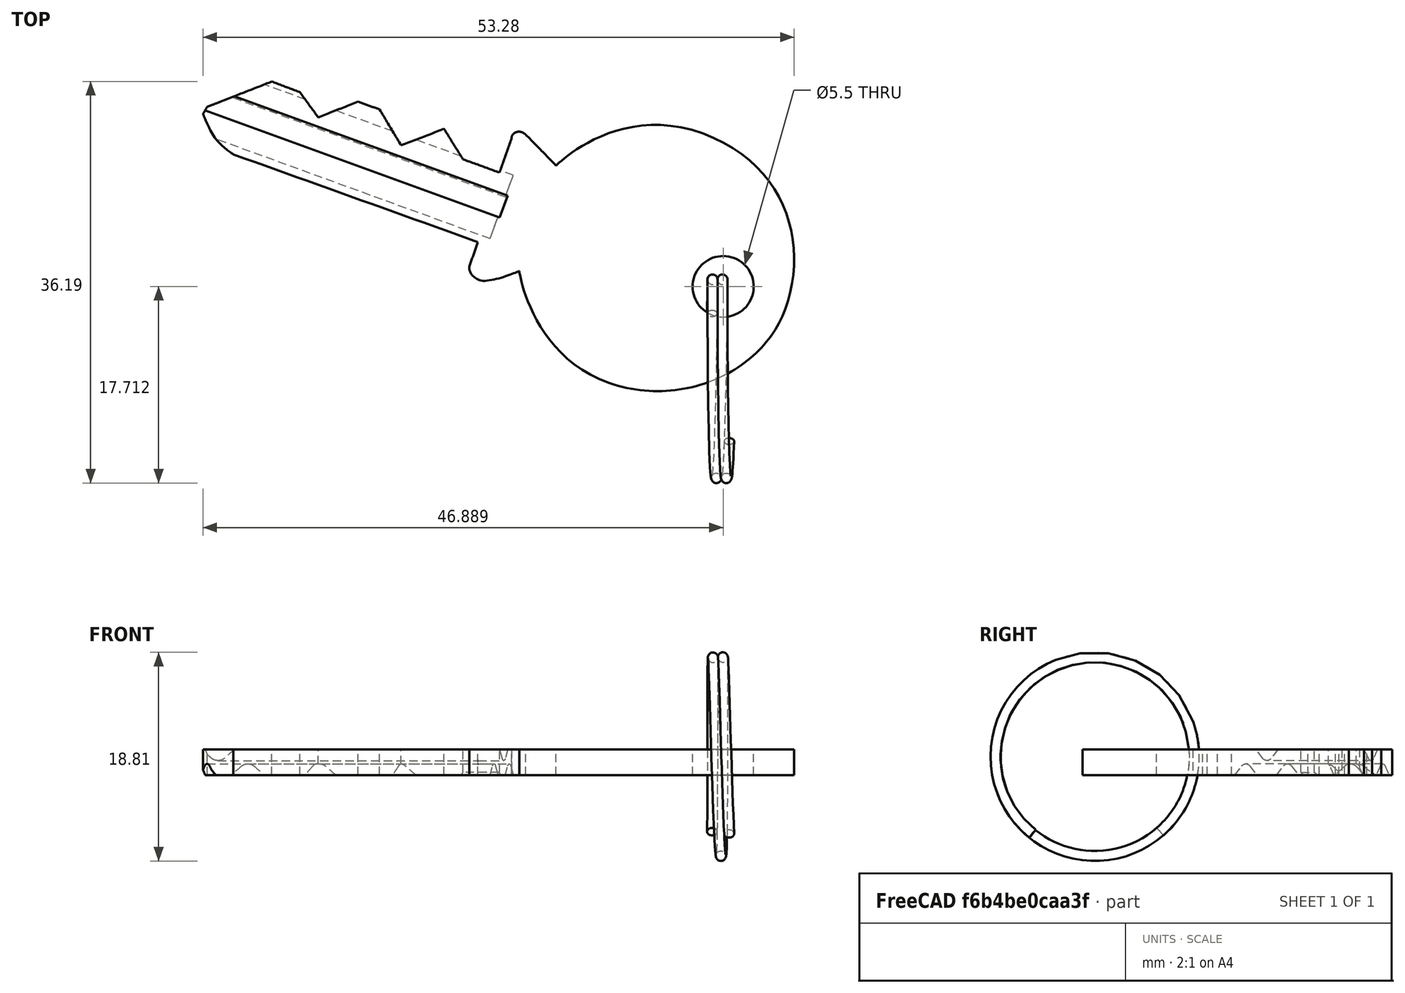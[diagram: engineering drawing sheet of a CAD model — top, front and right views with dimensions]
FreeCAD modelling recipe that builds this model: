
FCSTD DOCUMENT  (FreeCAD 0.16R6707 (Git))
Label: Llavero Modik
License: CreativeCommons Attribution-ShareAlike
LicenseURL: http://creativecommons.org/licenses/by-sa/4.0/
objects: Part::Feature×2, App::DocumentObjectGroup×1, Part::FeaturePython×1, Sketcher::SketchObject×1, PartDesign::Pad×1, Part::Cut×1
note: 7 computed .brp shape members not serialized (recipe doc carries the construction recipe); baked Part::Feature solids carry a one-line shape summary decoded from their .brp

FEATURE [Part::Feature] Sweep  label="key-ring-model-1"
  Placement = pos=(0.8,24.7546,1.6391) rot=(0.333333,0.881917,0.333333;1.67867rad)
  shape: bbox 3.25 x 27.05 x 26.3 mm, 4 faces (baked)
FEATURE [Part::Feature] Cut  label="key-model-1"
  Placement = pos=(7.53024,31.0266,0) rot=(0,0,1;2.79253rad)
  shape: bbox 54.12 x 28.51 x 2.3 mm, 44 faces (baked)
FEATURE [App::DocumentObjectGroup] Group  label="Assembly"
  Group = -> [Sweep,Cut]
FEATURE [Part::FeaturePython] Clone  label="Clone of logo_modik002"  # WARN: FeaturePython — macro-defined, semantics opaque (R4)
  Placement = pos=(8.69088,27.6503,-6.3277) rot=(1,0,0;1.5708rad)
  Scale = (0.3,0.3,0.3)
FEATURE [Sketcher::SketchObject] Sketch002
  ExternalGeometry = -> [Clone]
  Placement = pos=(8.69088,27.6503,1.99746) rot=(1,0,0;3.14159rad)
  Support = -> Clone [Face14]
  sketch-geometry (5):
    g0: Circle CenterX=-7.72299 CenterY=11.017 CenterZ=0 NormalX=0 NormalY=0 NormalZ=1 Radius=2.5
    g1: LineSegment [constr] StartX=-11.6513 StartY=10.6242 StartZ=0 EndX=-4.49716 EndY=17.7783 EndZ=0
    g2: LineSegment [constr] StartX=-9.37043 StartY=8.51696 StartZ=0 EndX=-3.44179 EndY=8.51696 EndZ=0
    g3: LineSegment [constr] StartX=-10.7182 StartY=11.5573 StartZ=0 EndX=-11.6904 EndY=12.3031 EndZ=0
    g4: LineSegment [constr] StartX=-7.74592 StartY=8.51696 StartZ=0 EndX=-7.74592 EndY=7.29162 EndZ=0
  constraints (13):
    c: Radius(g0) = 2.5
    c: Tangent(g2,g0)
    c: Tangent(g1,g0)
    c: Parallel(g1,g-3)
    c: PointOnObject(g3,g1)
    c: PointOnObject(g3,g-3)
    c: PointOnObject(g4,g2)
    c: PointOnObject(g4,g-4)
    c: Vertical(g4)
    c: Equal(g4,g3)
    c: Parallel(g2,g-4)
    c: Distance(g3) = 1.22534
    c: Distance(g4) = 1.22534
FEATURE [PartDesign::Pad] Pad
  Length = 10
  Length2 = 100
  Placement = pos=(8.69088,27.6503,-6.3277) rot=(1,0,0;1.5708rad)
  Sketch = -> Sketch002
  Type = 0
FEATURE [Part::Cut] Cut001  label="Llavero Modik"
  Base = -> Clone
  Placement = pos=(1,0,0) rot=(0,0,1;0rad)
  Tool = -> Pad
